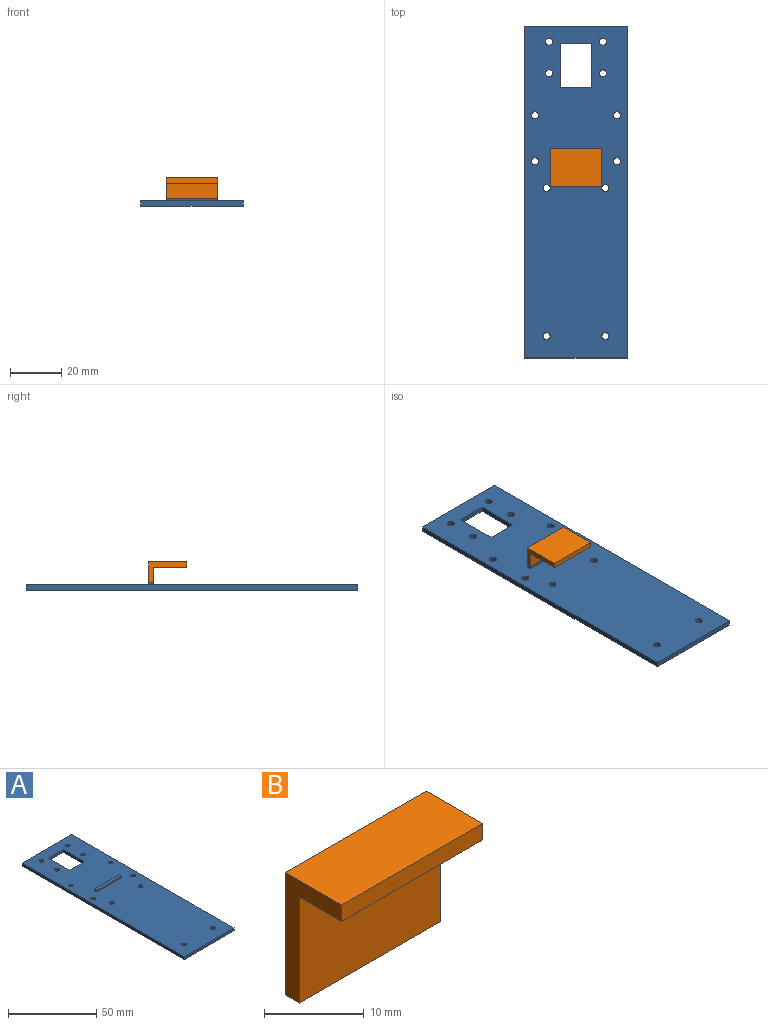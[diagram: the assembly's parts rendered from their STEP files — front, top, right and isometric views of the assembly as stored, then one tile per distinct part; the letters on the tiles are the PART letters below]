
ASSEMBLY  parts=2 mates=1
PART A: 27 faces, bbox 40x130x3 mm
  f0: plane 130x40mm, normal (0,0,1), area 4884.7mm2, adj f1,f2,f3,f4,f5,f6,f7,f8
  f1: plane 12x2mm, normal (0,-1,0), area 24mm2, adj f0,f2,f13,f21
  f2: plane 17x2mm, normal (-1,0,0), area 34mm2, adj f0,f1,f3,f21
  f3: plane 12x2mm, normal (0,1,0), area 24mm2, adj f0,f2,f13,f21
  f4: plane 130x2mm, normal (-1,0,0), area 260mm2, adj f0,f5,f19,f21
  f5: plane 40x2mm, normal (0,-1,0), area 80mm2, adj f0,f4,f6,f21
  f6: plane 130x2mm, normal (1,0,0), area 260mm2, adj f0,f5,f19,f21
  f7: cylinder r=1.38mm len=2.75mm, axis (0,0,-1), area 17.3mm2, adj f0,f21
  f8: cylinder r=1.38mm len=2.75mm, axis (0,0,-1), area 17.3mm2, adj f0,f21
  f9: cylinder r=1.38mm len=2.75mm, axis (0,0,-1), area 17.3mm2, adj f0,f21
  f10: cylinder r=1.38mm len=2.75mm, axis (0,0,-1), area 17.3mm2, adj f0,f21
  f11: cylinder r=1.38mm len=2.75mm, axis (0,0,-1), area 17.3mm2, adj f0,f21
  f12: cylinder r=1.38mm len=2.75mm, axis (0,0,-1), area 17.3mm2, adj f0,f21
  f13: plane 17x2mm, normal (1,0,0), area 34mm2, adj f0,f1,f3,f21
  f14: cylinder r=1.38mm len=2.75mm, axis (0,0,-1), area 17.3mm2, adj f0,f21
  f15: cylinder r=1.38mm len=2.75mm, axis (0,0,-1), area 17.3mm2, adj f0,f21
  f16: cylinder r=1.38mm len=2.75mm, axis (0,0,-1), area 17.3mm2, adj f0,f21
  f17: cylinder r=1.38mm len=2.75mm, axis (0,0,-1), area 17.3mm2, adj f0,f21
  f18: cylinder r=1.38mm len=2.75mm, axis (0,0,-1), area 17.3mm2, adj f0,f21
  f19: plane 40x2mm, normal (0,1,0), area 80mm2, adj f0,f4,f6,f21
  f20: cylinder r=1.38mm len=2.75mm, axis (0,0,-1), area 17.3mm2, adj f0,f21
  f21: plane 130x40mm, normal (0,0,-1), area 4924.7mm2, adj f1,f2,f3,f4,f5,f6,f7,f8
  f22: plane 20x1mm, normal (0,-1,0), area 20mm2, adj f0,f23,f25,f26
  f23: plane 2x1mm, normal (1,0,0), area 2mm2, adj f0,f22,f24,f26
  f24: plane 20x1mm, normal (0,1,0), area 20mm2, adj f0,f23,f25,f26
  f25: plane 2x1mm, normal (-1,0,0), area 2mm2, adj f0,f22,f24,f26
  f26: plane 20x2mm, normal (0,0,1), area 40mm2, adj f22,f23,f24,f25
PART B: 8 faces, bbox 20x8x15 mm
  f0: plane 20x15mm, normal (0,1,0), area 300mm2, adj f1,f5,f6,f7
  f1: plane 20x8mm, normal (0,0,1), area 160mm2, adj f0,f2,f6,f7
  f2: plane 20x2mm, normal (0,-1,0), area 40mm2, adj f1,f3,f6,f7
  f3: plane 20x6mm, normal (0,0,-1), area 120mm2, adj f2,f4,f6,f7
  f4: plane 20x13mm, normal (0,-1,0), area 260mm2, adj f3,f5,f6,f7
  f5: plane 20x2mm, normal (0,0,-1), area 40mm2, adj f0,f4,f6,f7
  f6: plane 15x8mm, normal (1,0,0), area 42mm2, adj f0,f1,f2,f3,f4,f5
  f7: plane 15x8mm, normal (-1,0,0), area 42mm2, adj f0,f1,f2,f3,f4,f5
PLACE A t=(-15.05,47.36,-2.72)mm
PLACE B rot(axis=(0,0.71,0.71),180deg) t=(-5.05,64.4,1.08)mm
MATE fastened B.f2 <-> A.f26  axis (0,0,-1) through (-15.05,64.4,0.28)mm
